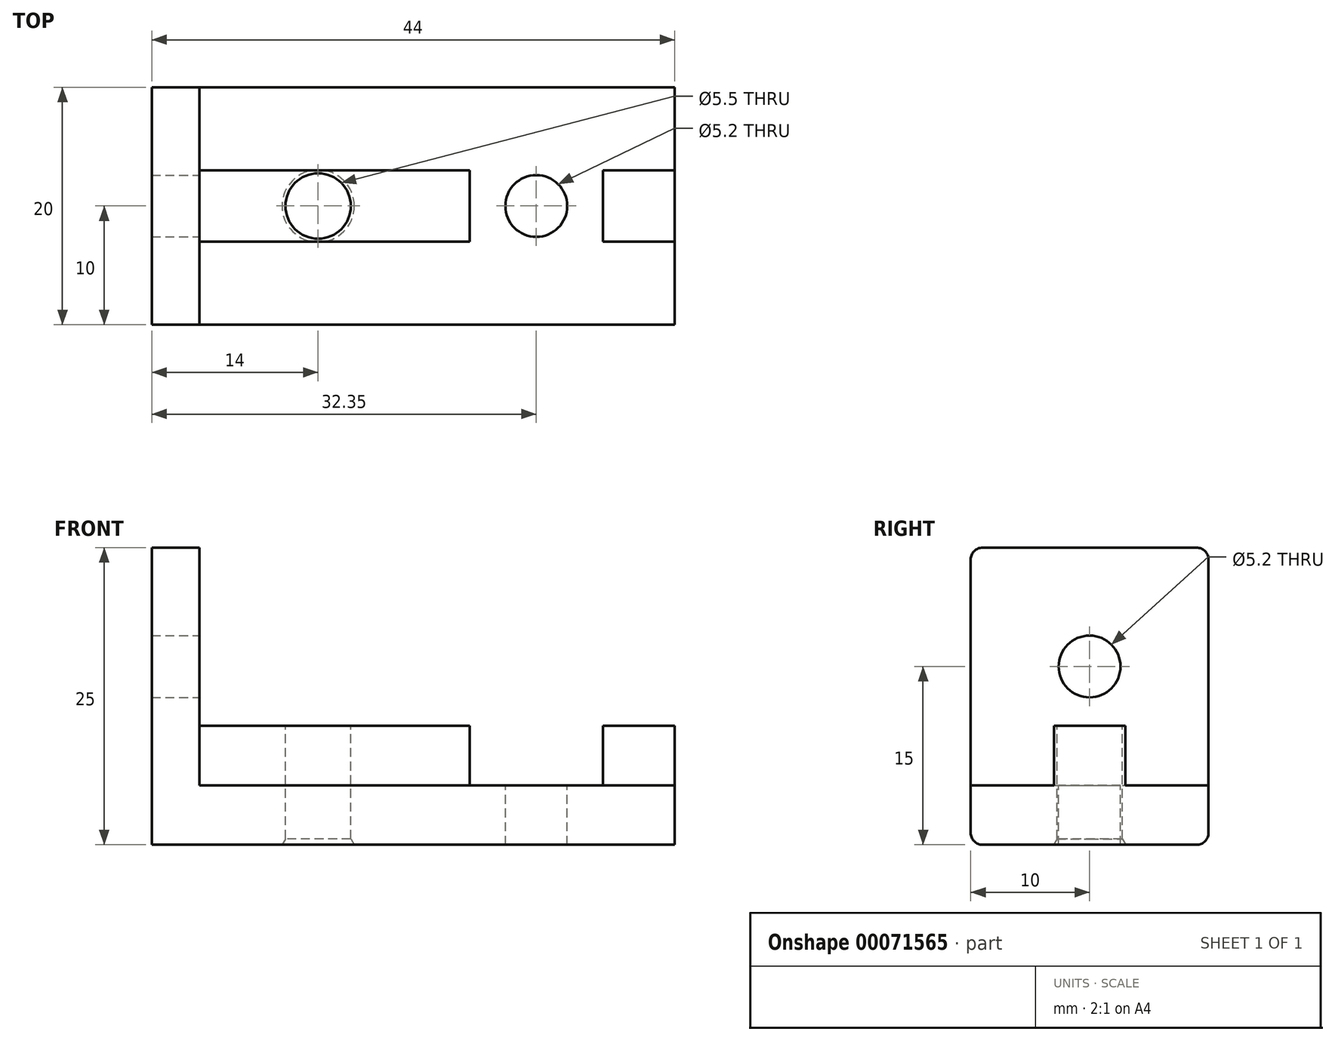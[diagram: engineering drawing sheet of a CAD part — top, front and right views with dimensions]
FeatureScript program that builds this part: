
annotation { "Feature Type Name" : "Feature", "Feature Type Description" : "" }
export const myFeature = defineFeature(function(context is Context, id is Id, definition is map)
    precondition{}
    {
        {
            var Q0;
            Q0=qCreatedBy(makeId("Top.planeOp"),FACE);
            var sketch = newSketch(context, id + "F0", { "sketchPlane" : qUnion([Q0])});
            skLineSegment(sketch, "E0.bottom", {"start": v(0, -10) * mm, "end": v(40, -10) * mm});
            skLineSegment(sketch, "E0.top", {"start": v(0, 10) * mm, "end": v(40, 10) * mm});
            skLineSegment(sketch, "E0.left", {"start": v(0, -10) * mm, "end": v(0, 10) * mm});
            skLineSegment(sketch, "E0.right", {"start": v(40, -10) * mm, "end": v(40, 10) * mm});
            skSolve(sketch);
        }
        {
            var Q0;
            Q0=qSketchRegion(id+"F0",true);
            extrude(context, id + "F1", {"entities" : qUnion([Q0]), "depth" : 5 * mm});
        }
        {
            var Q0;
            Q0=makeQuery(id+"F1.opExtrude","CAP_FACE",FACE,{"disambiguationData":[OSD([sQuery(id+"F0.wireOp",EDGE,"E0.bottom"),sQuery(id+"F0.wireOp",EDGE,"E0.top"),sQuery(id+"F0.wireOp",EDGE,"E0.left"),sQuery(id+"F0.wireOp",EDGE,"E0.right")])],"isStart":false});
            var sketch = newSketch(context, id + "F2", { "sketchPlane" : qUnion([Q0])});
            skLineSegment(sketch, "E1.bottom", {"start": v(0, 3) * mm, "end": v(40, 3) * mm});
            skLineSegment(sketch, "E1.top", {"start": v(0, -3) * mm, "end": v(40, -3) * mm});
            skLineSegment(sketch, "E1.left", {"start": v(0, 3) * mm, "end": v(0, -3) * mm});
            skLineSegment(sketch, "E1.right", {"start": v(40, 3) * mm, "end": v(40, -3) * mm});
            skSolve(sketch);
        }
        {
            var Q0;
            Q0=qSketchRegion(id+"F2",true);
            extrude(context, id + "F3", {"entities" : qUnion([Q0]), "operationType" : NewBodyOperationType.ADD, "depth" : 5 * mm});
        }
        {
            var Q0;
            Q0=makeQuery(id+"F3.opExtrude","CAP_FACE",FACE,{"disambiguationData":[OSD([sQuery(id+"F2.wireOp",EDGE,"E1.bottom"),sQuery(id+"F2.wireOp",EDGE,"E1.top"),sQuery(id+"F2.wireOp",EDGE,"E1.left"),sQuery(id+"F2.wireOp",EDGE,"E1.right")])],"isStart":false});
            var sketch = newSketch(context, id + "F4", { "sketchPlane" : qUnion([Q0])});
            skLineSegment(sketch, "E2", {"start": v(0, 0) * mm, "end": v(10, 0) * mm, "construction": true});
            skCircle(sketch, "E3", {"center": v(10, 0) * mm, "radius": 2.75 * mm});
            skSolve(sketch);
        }
        {
            var Q0;
            Q0=qSketchRegion(id+"F4",true);
            extrude(context, id + "F5", {"entities" : qUnion([Q0]), "operationType" : NewBodyOperationType.REMOVE, "oppositeDirection" : true, "depth" : 25 * mm});
        }
        {
            var Q0;
            Q0=makeQuery(id+"F3.opExtrude","CAP_FACE",FACE,{"disambiguationData":[OSD([sQuery(id+"F2.wireOp",EDGE,"E1.bottom"),sQuery(id+"F2.wireOp",EDGE,"E1.top"),sQuery(id+"F2.wireOp",EDGE,"E1.left"),sQuery(id+"F2.wireOp",EDGE,"E1.right")])],"isStart":false});
            var sketch = newSketch(context, id + "F6", { "sketchPlane" : qUnion([Q0])});
            skLineSegment(sketch, "E4.bottom", {"start": v(22.75, 3) * mm, "end": v(33.95, 3) * mm});
            skLineSegment(sketch, "E4.top", {"start": v(22.75, -3) * mm, "end": v(33.95, -3) * mm});
            skLineSegment(sketch, "E4.left", {"start": v(22.75, 3) * mm, "end": v(22.75, -3) * mm});
            skLineSegment(sketch, "E4.right", {"start": v(33.95, 3) * mm, "end": v(33.95, -3) * mm});
            skLineSegment(sketch, "E5", {"start": v(12.75, 0) * mm, "end": v(22.75, 0) * mm, "construction": true});
            skSolve(sketch);
        }
        {
            var Q0;
            Q0=qSketchRegion(id+"F6",true);
            var Q1;
            {var subQ0=sQuery(id+"F0.wireOp",EDGE,"E0.right");var subQ1=sQuery(id+"F0.wireOp",EDGE,"E0.left");var subQ2=sQuery(id+"F0.wireOp",EDGE,"E0.top");Q1=makeQuery(id+"F3.boolean.opBoolean","SPLIT",FACE,{"disambiguationData":[TD([makeQuery(id+"F1.opExtrude","SWEPT_FACE",FACE,{"disambiguationData":[OSD([subQ2])]})])],"derivedFrom":makeQuery(id+"F1.opExtrude","CAP_FACE",FACE,{"disambiguationData":[OSD([sQuery(id+"F0.wireOp",EDGE,"E0.bottom"),subQ2,subQ1,subQ0])],"isStart":false})});}
            extrude(context, id + "F7", {"entities" : qUnion([Q0]), "operationType" : NewBodyOperationType.REMOVE, "endBound" : BoundingType.UP_TO_SURFACE, "oppositeDirection" : true, "endBoundEntityFace" : qUnion([Q1]), "depth" : 25 * mm});
        }
        {
            var Q0;
            {var subQ0=sQuery(id+"F0.wireOp",EDGE,"E0.right");var subQ3=sQuery(id+"F0.wireOp",EDGE,"E0.left");var subQ5=sQuery(id+"F0.wireOp",EDGE,"E0.top");var subQ7=sQuery(id+"F0.wireOp",EDGE,"E0.bottom");var subQ8=makeQuery(id+"F1.opExtrude","CAP_FACE",FACE,{"disambiguationData":[OSD([subQ7,subQ5,subQ3,subQ0])],"isStart":false});Q0=makeQuery(id+"F7.boolean.opBoolean","MERGE",FACE,{"derivedFrom":[makeQuery(id+"F3.boolean.opBoolean","SPLIT",FACE,{"disambiguationData":[TD([makeQuery(id+"F1.opExtrude","SWEPT_FACE",FACE,{"disambiguationData":[OSD([subQ7])]})])],"derivedFrom":subQ8}),makeQuery(id+"F3.boolean.opBoolean","SPLIT",FACE,{"disambiguationData":[TD([makeQuery(id+"F1.opExtrude","SWEPT_FACE",FACE,{"disambiguationData":[OSD([subQ5])]})])],"derivedFrom":subQ8})],"fromTools":[makeQuery(id+"F7.opExtrude","CAP_FACE",FACE,{"disambiguationData":[OSD([sQuery(id+"F6.wireOp",EDGE,"E4.bottom"),sQuery(id+"F6.wireOp",EDGE,"E4.top"),sQuery(id+"F6.wireOp",EDGE,"E4.left"),sQuery(id+"F6.wireOp",EDGE,"E4.right")])],"isStart":false})]});}
            var sketch = newSketch(context, id + "F8", { "sketchPlane" : qUnion([Q0])});
            skLineSegment(sketch, "E6", {"start": v(22.75, 0) * mm, "end": v(33.95, 0) * mm, "construction": true});
            skCircle(sketch, "E7", {"center": v(28.35, 0) * mm, "radius": 2.6 * mm});
            skSolve(sketch);
        }
        {
            var Q0;
            Q0=qSketchRegion(id+"F8",true);
            extrude(context, id + "F9", {"entities" : qUnion([Q0]), "operationType" : NewBodyOperationType.REMOVE, "endBound" : BoundingType.UP_TO_NEXT, "oppositeDirection" : true, "depth" : 25 * mm});
        }
        {
            var Q0;
            Q0=makeQuery(id+"F3.boolean.opBoolean","MERGE",FACE,{"derivedFrom":[makeQuery(id+"F1.opExtrude","SWEPT_FACE",FACE,{"disambiguationData":[OSD([sQuery(id+"F0.wireOp",EDGE,"E0.left")])]}),makeQuery(id+"F3.opExtrude","SWEPT_FACE",FACE,{"disambiguationData":[OSD([sQuery(id+"F2.wireOp",EDGE,"E1.left")])]})]});
            var sketch = newSketch(context, id + "F10", { "sketchPlane" : qUnion([Q0])});
            skLineSegment(sketch, "E8.bottom", {"start": v(-10, 0) * mm, "end": v(10, 0) * mm});
            skLineSegment(sketch, "E8.top", {"start": v(-10, 25) * mm, "end": v(10, 25) * mm});
            skLineSegment(sketch, "E8.left", {"start": v(-10, 0) * mm, "end": v(-10, 25) * mm});
            skLineSegment(sketch, "E8.right", {"start": v(10, 0) * mm, "end": v(10, 25) * mm});
            skCircle(sketch, "E9", {"center": v(0, 15) * mm, "radius": 2.6 * mm});
            skLineSegment(sketch, "E10", {"start": v(0, 15) * mm, "end": v(0, 25) * mm, "construction": true});
            skSolve(sketch);
        }
        {
            var Q0;
            {var subQ11=sQuery(id+"F10.wireOp",EDGE,"E8.top");Q0=makeQuery(id+"F10.imprint","IMPRINT",FACE,{"disambiguationData":[TD([[makeQuery(id+"F10.imprint","IMPRINT",EDGE,{"derivedFrom":subQ11}),-1.0]])]});}
            var Q1;
            {var subQ4=sQuery(id+"F10.wireOp",EDGE,"E8.bottom");Q1=makeQuery(id+"F10.imprint","IMPRINT",FACE,{"disambiguationData":[TD([[makeQuery(id+"F10.imprint","IMPRINT",EDGE,{"derivedFrom":subQ4}),-1.0]])]});}
            extrude(context, id + "F11", {"entities" : qUnion([Q0, Q1]), "operationType" : NewBodyOperationType.ADD, "depth" : 4 * mm});
        }
        {
            var Q0;
            Q0=makeQuery(id+"F11.opExtrude","SWEPT_EDGE",EDGE,{"disambiguationData":[OSD([sQuery(id+"F10.wireOp",EDGE,"E8.top"),sQuery(id+"F10.wireOp",EDGE,"E8.right")])]});
            var Q1;
            Q1=makeQuery(id+"F11.opExtrude","SWEPT_EDGE",EDGE,{"disambiguationData":[OSD([sQuery(id+"F10.wireOp",EDGE,"E8.top"),sQuery(id+"F10.wireOp",EDGE,"E8.left")])]});
            var Q2;
            Q2=makeQuery(id+"F11.boolean.opBoolean","MERGE",EDGE,{"derivedFrom":[makeQuery(id+"F1.opExtrude","CAP_EDGE",EDGE,{"disambiguationData":[OSD([sQuery(id+"F0.wireOp",EDGE,"E0.bottom")])],"isStart":true}),makeQuery(id+"F11.opExtrude","SWEPT_EDGE",EDGE,{"disambiguationData":[OSD([sQuery(id+"F10.wireOp",EDGE,"E8.bottom"),sQuery(id+"F10.wireOp",EDGE,"E8.right")])]})]});
            var Q3;
            Q3=makeQuery(id+"F11.boolean.opBoolean","MERGE",EDGE,{"derivedFrom":[makeQuery(id+"F1.opExtrude","CAP_EDGE",EDGE,{"disambiguationData":[OSD([sQuery(id+"F0.wireOp",EDGE,"E0.top")])],"isStart":true}),makeQuery(id+"F11.opExtrude","SWEPT_EDGE",EDGE,{"disambiguationData":[OSD([sQuery(id+"F10.wireOp",EDGE,"E8.bottom"),sQuery(id+"F10.wireOp",EDGE,"E8.left")])]})]});
            fillet(context, id + "F12", {"entities" : qUnion([Q0, Q1, Q2, Q3]), "radius" : 1 * mm, "tangentPropagation" : true, "allowEdgeOverflow" : false});
        }
        {
            var Q0;
            Q0=makeQuery(id+"F5.boolean.opBoolean","INTERSECT",EDGE,{"derivedFrom":[makeQuery(id+"F1.opExtrude","CAP_FACE",FACE,{"disambiguationData":[OSD([sQuery(id+"F0.wireOp",EDGE,"E0.bottom"),sQuery(id+"F0.wireOp",EDGE,"E0.top"),sQuery(id+"F0.wireOp",EDGE,"E0.left"),sQuery(id+"F0.wireOp",EDGE,"E0.right")])],"isStart":true}),makeQuery(id+"F5.opExtrude","SWEPT_FACE",FACE,{"disambiguationData":[OSD([sQuery(id+"F4.wireOp",EDGE,"E3")])]})]});
            var Q1;
            Q1=makeQuery(id+"F5.boolean.opBoolean","INTERSECT",EDGE,{"derivedFrom":[makeQuery(id+"F1.opExtrude","CAP_FACE",FACE,{"disambiguationData":[OSD([sQuery(id+"F0.wireOp",EDGE,"E0.bottom"),sQuery(id+"F0.wireOp",EDGE,"E0.top"),sQuery(id+"F0.wireOp",EDGE,"E0.left"),sQuery(id+"F0.wireOp",EDGE,"E0.right")])],"isStart":true}),makeQuery(id+"F5.opExtrude","SWEPT_FACE",FACE,{"disambiguationData":[OSD([sQuery(id+"F4.wireOp",EDGE,"60a69525-9c60-453c-9632-db69a013bd03")])]})]});
            var Q2;
            Q2=makeQuery(id+"F5.boolean.opBoolean","INTERSECT",EDGE,{"derivedFrom":[makeQuery(id+"F1.opExtrude","CAP_FACE",FACE,{"disambiguationData":[OSD([sQuery(id+"F0.wireOp",EDGE,"E0.bottom"),sQuery(id+"F0.wireOp",EDGE,"E0.top"),sQuery(id+"F0.wireOp",EDGE,"E0.left"),sQuery(id+"F0.wireOp",EDGE,"E0.right")])],"isStart":true}),makeQuery(id+"F5.opExtrude","SWEPT_FACE",FACE,{"disambiguationData":[OSD([sQuery(id+"F4.wireOp",EDGE,"09b359c9-9fed-4956-9e02-5c3cf4e6a809")])]})]});
            chamfer(context, id + "F13", {"entities" : qUnion([Q0, Q1, Q2]), "chamferType" : ChamferType.OFFSET_ANGLE, "width" : .5 * mm, "oppositeDirection" : true, "angle" : 30 * degree, "tangentPropagation" : true});
        }
    });
